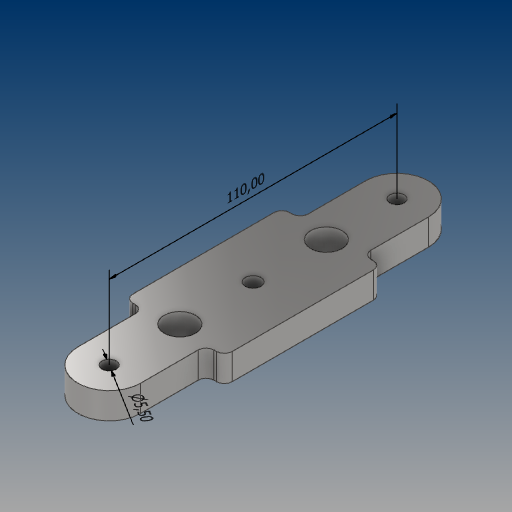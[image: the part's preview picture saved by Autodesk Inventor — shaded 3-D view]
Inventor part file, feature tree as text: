
AUTODESK INVENTOR PART (.ipt)
format: ipt  version: 2021 (Build 250183000, 183)  size: 173,568 bytes
history: native  units: mm
features: sketch x4, other x3, extrude x2, hole x2, fillet x1, projected_geometry x1
ambient origin geometry x8: Origin, YZ Plane, XZ Plane, XY Plane, X Axis, Y Axis, Z Axis, Center Point
bodies: Solid1 (feature_tree)
feature tree (13):
  other  "Annotations"
  extrude  "Extrusion1"  Depth=60.0mm
  hole  "Hole1"  [1 undecoded]
  fillet  "Fillet1"  Radius=10.0mm
  hole  "Hole2"  [1 undecoded]
  extrude  "Extrusion2"  Depth=6.0mm
  sketch  "Sketch1"  dims[d0=60.0mm d1=110.0mm]
  sketch  "Sketch2"  dims[d2=12.0mm d3=38.0mm d4=10.0mm d5=0.0mm]
  projected_geometry  "Projected Loop1"
  sketch  "Sketch3"  dims[d6=56.0mm]
  sketch  "Sketch4"  dims[d7=12.0mm d8=6.0mm d9=4.0mm d10=2.0mm d11=90.0deg d12=8.0mm d13=20.594885mm d14=3.0mm d15=5.5mm d16=6.0mm d17=4.0mm d18=2.0mm d19=90.0deg d20=8.0mm d21=20.594885mm d22=6.0mm d23=7.5mm d24=0.0mm d25=117.616421mm d26=118.351598mm d27=110.0mm d28=18.385343mm d29=5.5mm]
  other  "Linear Dimension 1"
  other  "Diameter Dimension 1"
note: 2 required parameter values undecoded (feature->parameter linkage not recoverable at this tier; creation-order binding heuristic only, values carry confidence <= 0.55)
